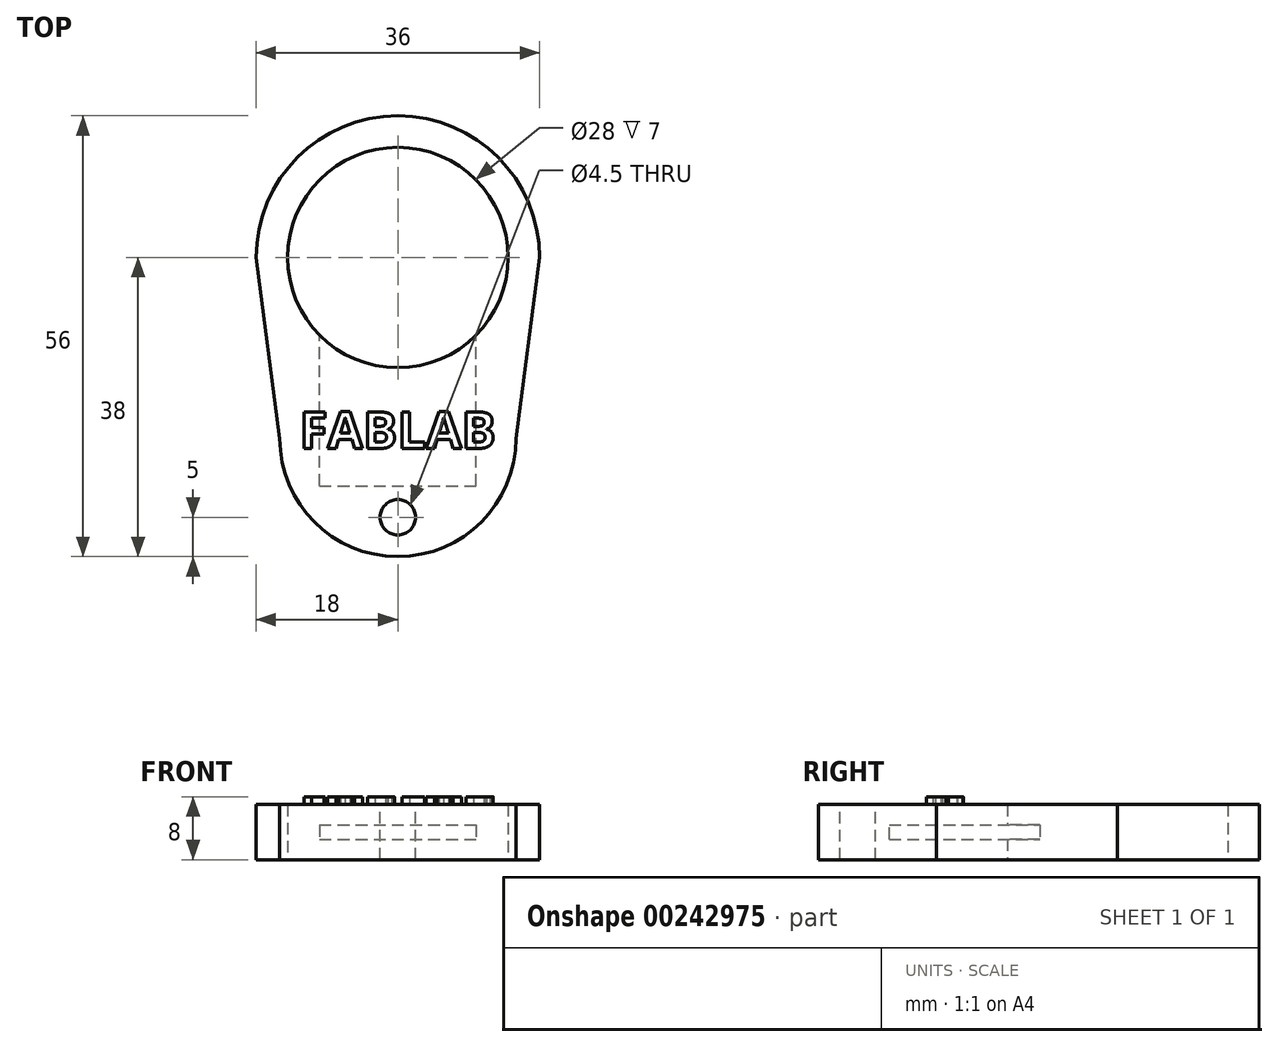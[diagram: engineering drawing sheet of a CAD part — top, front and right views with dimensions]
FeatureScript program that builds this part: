
annotation { "Feature Type Name" : "Feature", "Feature Type Description" : "" }
export const myFeature = defineFeature(function(context is Context, id is Id, definition is map)
    precondition{}
    {
        {
            var Q0;
            Q0=qCreatedBy(makeId("Top.planeOp"),FACE);
            var sketch = newSketch(context, id + "F0", { "sketchPlane" : qUnion([Q0])});
            skCircle(sketch, "E0", {"center": v(0, 0) * mm, "radius": 14 * mm});
            skArc(sketch, "E1", {"start": v(18, 0) * mm, "mid": v(0, 18) * mm, "end": v(-18, 0) * mm});
            skArc(sketch, "E2", {"start": v(-15, -23) * mm, "mid": v(0, -38) * mm, "end": v(15, -23) * mm});
            skLineSegment(sketch, "E3", {"start": v(-24.34, -23) * mm, "end": v(26.16, -23) * mm, "construction": true});
            skPoint(sketch, "E4", {"position": v(-18, 0) * mm});
            skPoint(sketch, "E5", {"position": v(18, 0) * mm});
            skPoint(sketch, "E6", {"position": v(15, -23) * mm});
            skPoint(sketch, "E7", {"position": v(-15, -23) * mm});
            skLineSegment(sketch, "E8", {"start": v(-18, 0) * mm, "end": v(-15, -23) * mm});
            skLineSegment(sketch, "E9", {"start": v(18, 0) * mm, "end": v(15, -23) * mm});
            skSolve(sketch);
        }
        {
            var Q0;
            Q0=makeQuery(id+"F0.imprint","IMPRINT",FACE,{"disambiguationData":[TD([[makeQuery(id+"F0.imprint","IMPRINT",EDGE,{"derivedFrom":sQuery(id+"F0.wireOp",EDGE,"E0")}),-1.0]])]});
            extrude(context, id + "F1", {"entities" : qUnion([Q0]), "depth" : 7 * mm});
        }
        {
            var Q0;
            Q0=qCreatedBy(makeId("Front.planeOp"),FACE);
            var sketch = newSketch(context, id + "F2", { "sketchPlane" : qUnion([Q0])});
            skLineSegment(sketch, "E10.bottom", {"start": v(-9.95, 2.6) * mm, "end": v(9.95, 2.6) * mm});
            skLineSegment(sketch, "E10.top", {"start": v(-9.95, 4.4) * mm, "end": v(9.95, 4.4) * mm});
            skLineSegment(sketch, "E10.left", {"start": v(-9.95, 2.6) * mm, "end": v(-9.95, 4.4) * mm});
            skLineSegment(sketch, "E10.right", {"start": v(9.95, 2.6) * mm, "end": v(9.95, 4.4) * mm});
            skPoint(sketch, "E10.middle", {"position": v(0, 3.5) * mm});
            skSolve(sketch);
        }
        {
            var Q0;
            Q0=makeQuery(id+"F2.imprint","IMPRINT",FACE,{"disambiguationData":[TD([[makeQuery(id+"F2.imprint","IMPRINT",EDGE,{"derivedFrom":sQuery(id+"F2.wireOp",EDGE,"E10.bottom")}),1.0]])]});
            extrude(context, id + "F3", {"entities" : qUnion([Q0]), "operationType" : NewBodyOperationType.REMOVE, "depth" : 29 * mm});
        }
        {
            var Q0;
            Q0=makeQuery(id+"F1.opExtrude","CAP_FACE",FACE,{"disambiguationData":[OSD([sQuery(id+"F0.wireOp",EDGE,"E0"),sQuery(id+"F0.wireOp",EDGE,"E1"),sQuery(id+"F0.wireOp",EDGE,"E2"),sQuery(id+"F0.wireOp",EDGE,"E8"),sQuery(id+"F0.wireOp",EDGE,"E9")])],"isStart":false});
            var sketch = newSketch(context, id + "F4", { "sketchPlane" : qUnion([Q0])});
            skCircle(sketch, "E11", {"center": v(0, -33) * mm, "radius": 2.25 * mm});
            skLineSegment(sketch, "E12", {"start": v(0, 0) * mm, "end": v(0, -38) * mm, "construction": true});
            skSolve(sketch);
        }
        {
            var Q0;
            Q0=makeQuery(id+"F1.opExtrude","CAP_FACE",FACE,{"disambiguationData":[OSD([sQuery(id+"F0.wireOp",EDGE,"E0"),sQuery(id+"F0.wireOp",EDGE,"E1"),sQuery(id+"F0.wireOp",EDGE,"E2"),sQuery(id+"F0.wireOp",EDGE,"E8"),sQuery(id+"F0.wireOp",EDGE,"E9")])],"isStart":false});
            var sketch = newSketch(context, id + "F5", { "sketchPlane" : qUnion([Q0])});
            skSolve(sketch);
        }
        {
            var Q0;
            Q0 = qSketchRegion(id + "F4", true);
            extrude(context, id + "F6", {"entities" : qUnion([Q0]), "operationType" : NewBodyOperationType.REMOVE, "oppositeDirection" : true, "depth" : 25 * mm});
        }
        {
            var Q0;
            Q0=makeQuery(id+"F5.imprint","IMPRINT",FACE,{"disambiguationData":[TD([[makeQuery(id+"F5.imprint","IMPRINT",EDGE,{"derivedFrom":makeQuery(id+"F1.opExtrude","CAP_EDGE",EDGE,{"disambiguationData":[OSD([sQuery(id+"F0.wireOp",EDGE,"E0")])],"isStart":false})}),-1.0]])]});
            var sketch = newSketch(context, id + "F7", { "sketchPlane" : qUnion([Q0])});
            skText(sketch, "E13", { "text": "FABLAB", "fontName": "OpenSans-Bold.ttf"});
            skPoint(sketch, "E14", {"position": v(-12.5, -21.9) * mm});
            skPoint(sketch, "E15", {"position": v(0, -19.57) * mm});
            const initialGuessF7  = {"E13": [-0.0125, -0.02425, 1, 0, 0.00468]};
            skSetInitialGuess(sketch, initialGuessF7);
            skSolve(sketch);
        }
        {
            var Q0;
            Q0 = qSketchRegion(id + "F7", true);
            extrude(context, id + "F8", {"entities" : qUnion([Q0]), "operationType" : NewBodyOperationType.ADD, "depth" : 1 * mm});
        }
    });
